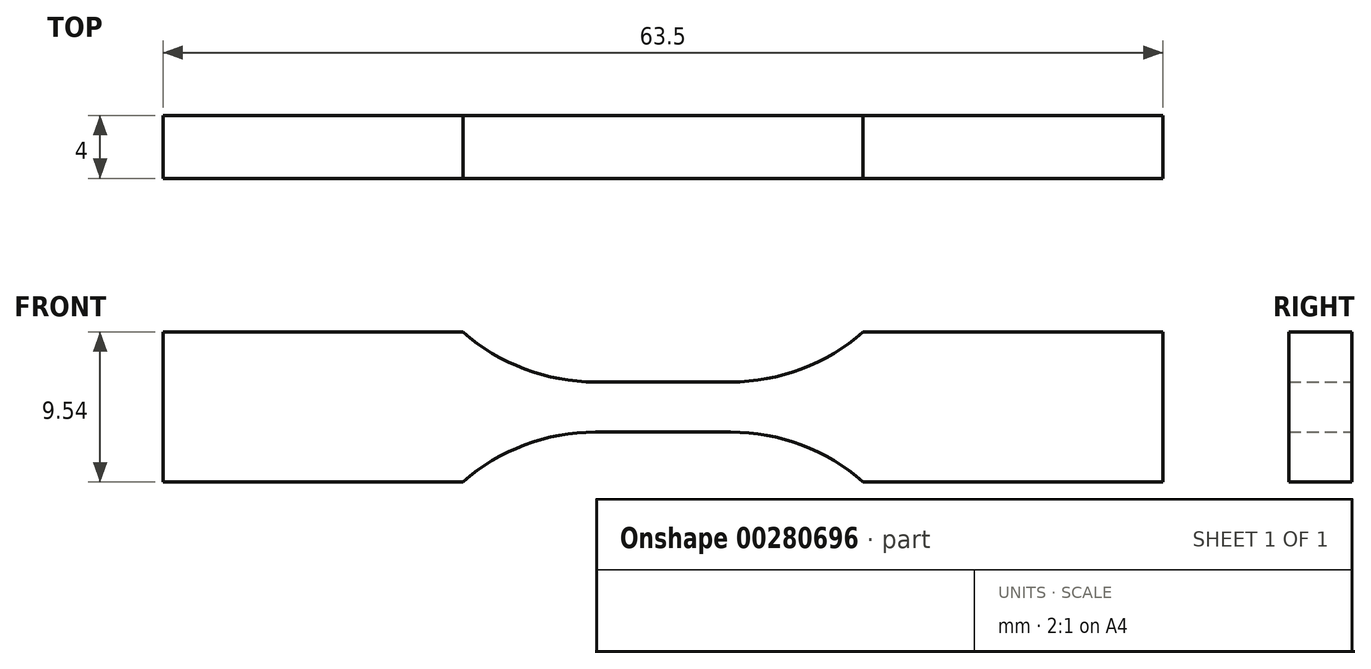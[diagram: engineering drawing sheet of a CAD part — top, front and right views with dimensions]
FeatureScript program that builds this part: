
annotation { "Feature Type Name" : "Feature", "Feature Type Description" : "" }
export const myFeature = defineFeature(function(context is Context, id is Id, definition is map)
    precondition{}
    {
        {
            var Q0;
            Q0=qCreatedBy(makeId("Front.planeOp"),FACE);
            var sketch = newSketch(context, id + "F0", { "sketchPlane" : qUnion([Q0])});
            skLineSegment(sketch, "E0", {"start": v(0, 1.59) * mm, "end": v(4.3, 1.59) * mm});
            skArc(sketch, "E1", {"start": v(4.3, 1.6) * mm, "mid": v(8.79, 2.41) * mm, "end": v(12.7, 4.77) * mm});
            skLineSegment(sketch, "E2", {"start": v(12.7, 4.77) * mm, "end": v(31.75, 4.77) * mm});
            skLineSegment(sketch, "E3.MirrorCS", {"start": v(0, -1.59) * mm, "end": v(4.3, -1.59) * mm});
            skLineSegment(sketch, "E4.MirrorCS", {"start": v(12.7, -4.76) * mm, "end": v(31.75, -4.76) * mm});
            skArc(sketch, "E5.MirrorCS", {"start": v(4.3, -1.6) * mm, "mid": v(8.79, -2.41) * mm, "end": v(12.7, -4.77) * mm});
            skLineSegment(sketch, "E6.MirrorCS", {"start": v(12.7, -4.77) * mm, "end": v(31.75, -4.77) * mm});
            skLineSegment(sketch, "E7.MirrorCS", {"start": v(-12.7, 4.77) * mm, "end": v(-31.75, 4.77) * mm});
            skLineSegment(sketch, "E8.MirrorCS", {"start": v(-12.7, -4.76) * mm, "end": v(-31.75, -4.76) * mm});
            skLineSegment(sketch, "E9.MirrorCS", {"start": v(-12.7, 4.76) * mm, "end": v(-31.75, 4.76) * mm});
            skLineSegment(sketch, "E10.MirrorCS", {"start": v(-12.7, -4.77) * mm, "end": v(-31.75, -4.77) * mm});
            skArc(sketch, "E11.MirrorCS", {"start": v(-4.3, -1.6) * mm, "mid": v(-8.79, -2.41) * mm, "end": v(-12.7, -4.77) * mm});
            skArc(sketch, "E12.MirrorCS", {"start": v(-4.3, 1.6) * mm, "mid": v(-8.79, 2.41) * mm, "end": v(-12.7, 4.77) * mm});
            skLineSegment(sketch, "E13.MirrorCS", {"start": v(0, 1.59) * mm, "end": v(-4.3, 1.59) * mm});
            skLineSegment(sketch, "E14.MirrorCS", {"start": v(0, -1.6) * mm, "end": v(-4.3, -1.6) * mm});
            skLineSegment(sketch, "E15", {"start": v(-31.75, 4.76) * mm, "end": v(-31.75, -4.76) * mm});
            skLineSegment(sketch, "E16", {"start": v(31.75, 4.76) * mm, "end": v(31.75, -4.76) * mm});
            skSolve(sketch);
        }
        {
            var Q0;
            Q0 = qSketchRegion(id + "F0", true);
            extrude(context, id + "F1", {"entities" : qUnion([Q0]), "depth" : 4 * mm});
        }
    });
